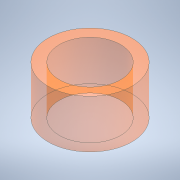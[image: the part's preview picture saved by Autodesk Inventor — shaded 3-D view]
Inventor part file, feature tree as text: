
AUTODESK INVENTOR PART (.ipt)
format: ipt  version: 2020 (Build 240168000, 168)  size: 109,568 bytes
history: native  units: in
note: dims shown in document units (in); Inventor stores cm internally (conversion verified against a paired STEP export)
features: extrude x1, sketch x1
ambient origin geometry x8: Origin, YZ Plane, XZ Plane, XY Plane, X Axis, Y Axis, Z Axis, Center Point
bodies: Solid1 (feature_tree)
feature tree (2):
  extrude  "Extrusion1"  Depth=1.1811in
  sketch  "Sketch1"  dims[d0=2.0472in d1=1.4961in d2=1.1811in d3=0.0in]
